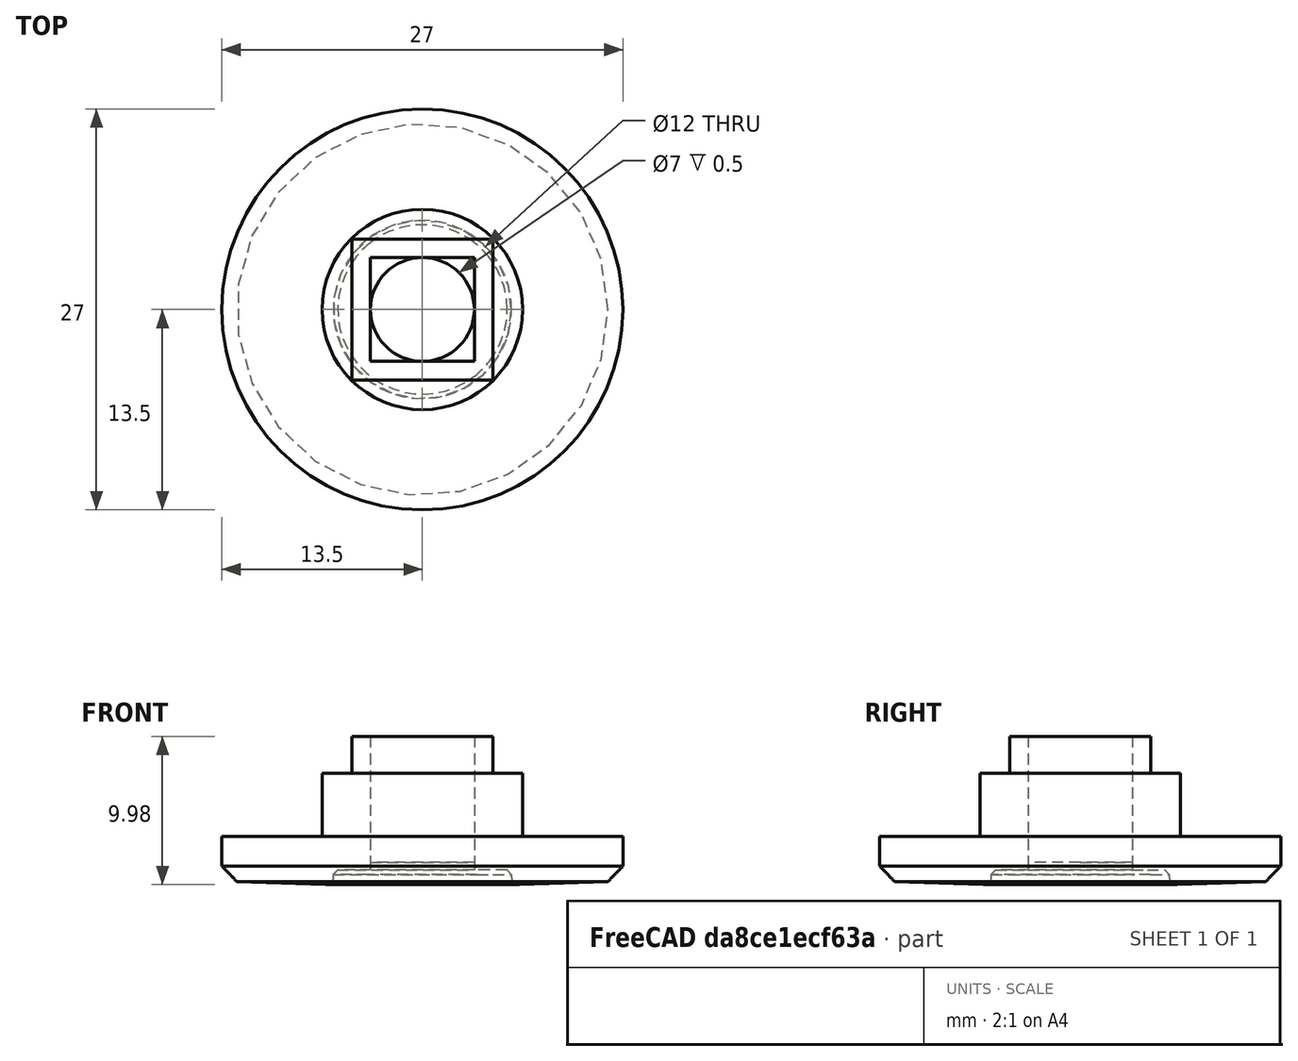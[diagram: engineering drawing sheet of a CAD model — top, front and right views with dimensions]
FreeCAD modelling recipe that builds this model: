
FCSTD DOCUMENT  (FreeCAD 0.19R24276 (Git))
Label: espaciador alojamiento junta goma
License: All rights reserved
LicenseURL: http://en.wikipedia.org/wiki/All_rights_reserved
objects: TechDraw::DrawViewDimension×10, TechDraw::DrawProjGroupItem×3, Part::Box×2, Part::Cut×2, Part::Chamfer×2, TechDraw::DrawSVGTemplate×2, TechDraw::DrawViewPart×2, TechDraw::DrawPage×2, Sketcher::SketchObject×1, PartDesign::Revolution×1, Part::MultiFuse×1, Part::Cylinder×1, Part::Fillet×1, TechDraw::DrawProjGroup×1, TechDraw::DrawViewAnnotation×1
note: 12 computed .brp shape members not serialized (recipe doc carries the construction recipe); baked Part::Feature solids carry a one-line shape summary decoded from their .brp

FEATURE [Sketcher::SketchObject] Sketch
  FullyConstrained = false
  MapMode = 5
  Placement = pos=(0,0,0) rot=(1,0,0;1.5708rad)
  sketch-geometry (8):
    g0: LineSegment StartX=0 StartY=0 StartZ=0 EndX=0 EndY=6.5 EndZ=0
    g1: LineSegment StartX=0 StartY=6.5 StartZ=0 EndX=6 EndY=6.5 EndZ=0
    g2: LineSegment StartX=6 StartY=6.5 StartZ=0 EndX=6 EndY=7.5 EndZ=0
    g3: LineSegment StartX=6 StartY=7.5 StartZ=0 EndX=13.5 EndY=7.23809 EndZ=0
    g4: LineSegment StartX=13.5 StartY=7.23809 StartZ=0 EndX=13.5 EndY=4.23809 EndZ=0
    g5: LineSegment StartX=13.5 StartY=4.23809 StartZ=0 EndX=6.75 EndY=4.23809 EndZ=0
    g6: LineSegment StartX=6.75 StartY=4.23809 StartZ=0 EndX=6.75 EndY=0 EndZ=0
    g7: LineSegment StartX=6.75 StartY=0 StartZ=0 EndX=0 EndY=0 EndZ=0
  constraints (23):
    c: Coincident(g0,g1)
    c: Coincident(g1,g2)
    c: Coincident(g2,g3)
    c: Coincident(g3,g4)
    c: Coincident(g4,g5)
    c: Coincident(g5,g6)
    c: Coincident(g6,g7)
    c: Angle(g3,g4) = 1.6057
    c: Vertical(g4)
    c: Horizontal(g1)
    c: Vertical(g2)
    c: DistanceY(g4,g4) = 3
    c: DistanceY(g2,g2) = 1
    c: Coincident(g0,g7)
    c: Coincident(g0,g-1)
    c: Vertical(g0)
    c: Horizontal(g7)
    c: Vertical(g6)
    c: DistanceY(g0,g0) = 6.5
    c: DistanceX(g1,g1) = 6
    c: DistanceX(g7,g7) = 6.75
    c: DistanceX(g5,g5) = 6.75
    c: Horizontal(g5)
FEATURE [PartDesign::Revolution] Revolution
  AllowMultiFace = false
  Angle = 360
  Axis = (0,0,1)
  Base = (0,0,0)
  Placement = pos=(0,0,0) rot=(1,0,0;1.5708rad)
  Profile = -> Sketch
  ReferenceAxis = -> Sketch [V_Axis]
  Reversed = true
FEATURE [Part::Box] Box  label="Cubo"
  AttacherType = Attacher::AttachEngine3D
  Height = 9
  Length = 9.5
  Placement = pos=(-4.75,-4.75,-2.5) rot=(0,0,1;0rad)
  Width = 9.5
FEATURE [Part::MultiFuse] Fusion
  Shapes = -> [Revolution,Box]
FEATURE [Part::Cylinder] Cylinder  label="Cilindro"
  Angle = 360
  AttacherType = Attacher::AttachEngine3D
  Height = 13
  Placement = pos=(0,0,-5) rot=(0,0,1;0rad)
  Radius = 3.5
FEATURE [Part::Box] Box001  label="Cubo001"
  AttacherType = Attacher::AttachEngine3D
  Height = 10.5
  Length = 7
  Placement = pos=(-3.5,-3.5,-4.5) rot=(0,0,1;0rad)
  Width = 7
FEATURE [Part::Cut] Cut
  Base = -> Fusion
  Tool = -> Box001
FEATURE [Part::Cut] Cut001
  Base = -> Cut
  Tool = -> Cylinder
FEATURE [Part::Chamfer] Chamfer
  Base = -> Cut001
  Edges = 1 edges r=0.3: [Edge5]
FEATURE [Part::Fillet] Fillet
  Base = -> Chamfer
  Edges = 1 edges r=0.5: [Edge3]
FEATURE [Part::Chamfer] Chamfer001
  Base = -> Fillet
  Edges = 1 edges r=1: [Edge27]
  Placement = pos=(0,0,0) rot=(1,0,0;3.14159rad)
FEATURE [TechDraw::DrawSVGTemplate] Template
  EditableTexts = Designed_by_Name=<owner>; Drawing_number=001; FC-Date=-; FC-SC=1:1; FC-SH=3/10; FC-Title=Spacer_O-ring; Subtitle=Espaciador Junta; Weight=<100gr
  Height = 210
  Orientation = 1
  Width = 297
FEATURE [TechDraw::DrawSVGTemplate] Template001
  EditableTexts = Designed_by_Name=<owner>; Drawing_number=001; FC-Date=-; FC-SC=4:1; FC-SH=4/10; FC-Title=Spacer_O-ring; Subtitle=Espaciador Junta; Weight=<100gr
  Height = 210
  Orientation = 1
  Width = 297
FEATURE [TechDraw::DrawViewPart] View
  CoarseView = false
  Direction = (0.577,-0.577,0.577)
  Focus = 100
  HardHidden = false
  IsoCount = 0
  IsoHidden = false
  IsoVisible = false
  LockPosition = false
  Perspective = false
  Rotation = 0
  Scale = 4
  ScaleType = 0
  SeamHidden = false
  SeamVisible = true
  SmoothHidden = false
  SmoothVisible = true
  Source = -> [Chamfer001]
  X = 201.279
  XDirection = (0.707,0.707,0)
  Y = 128.725
FEATURE [TechDraw::DrawViewPart] View001
  CoarseView = false
  Direction = (0.577,-0.577,0.577)
  Focus = 100
  HardHidden = false
  IsoCount = 0
  IsoHidden = false
  IsoVisible = false
  LockPosition = false
  Perspective = false
  Rotation = 0
  Scale = 4
  ScaleType = 0
  SeamHidden = false
  SeamVisible = true
  SmoothHidden = false
  SmoothVisible = true
  Source = -> [Chamfer001]
  X = 136.032
  XDirection = (0.707,0.707,0)
  Y = 120.195
FEATURE [TechDraw::DrawProjGroupItem] ProjItem  label="Front"
  CoarseView = false
  Direction = (0,-1,0)
  Focus = 100
  HardHidden = false
  IsoCount = 0
  IsoHidden = false
  IsoVisible = false
  LockPosition = true
  Perspective = false
  Rotation = 0
  RotationVector = (1,0,0)
  ScaleType = 2
  SeamHidden = false
  SeamVisible = true
  SmoothHidden = false
  SmoothVisible = true
  Source = -> [Chamfer001]
  Type = 0
  X = 0
  XDirection = (1,0,0)
  Y = 0
FEATURE [TechDraw::DrawProjGroupItem] ProjItem002  label="Top"
  CoarseView = false
  Direction = (0,0,1)
  Focus = 100
  HardHidden = false
  IsoCount = 0
  IsoHidden = false
  IsoVisible = false
  LockPosition = false
  Perspective = false
  Rotation = 0
  RotationVector = (1,0,0)
  ScaleType = 2
  SeamHidden = false
  SeamVisible = true
  SmoothHidden = false
  SmoothVisible = true
  Source = -> [Chamfer001]
  Type = 4
  X = 0
  XDirection = (1,0,0)
  Y = -41.9911
FEATURE [TechDraw::DrawProjGroupItem] ProjItem003  label="Bottom"
  CoarseView = false
  Direction = (0,0,-1)
  Focus = 100
  HardHidden = false
  IsoCount = 0
  IsoHidden = false
  IsoVisible = false
  LockPosition = false
  Perspective = false
  Rotation = 0
  RotationVector = (1,0,0)
  ScaleType = 2
  SeamHidden = false
  SeamVisible = true
  SmoothHidden = false
  SmoothVisible = true
  Source = -> [Chamfer001]
  Type = 5
  X = 0
  XDirection = (1,0,0)
  Y = 42.0089
FEATURE [TechDraw::DrawProjGroup] ProjGroup
  Anchor = -> ProjItem
  AutoDistribute = true
  LockPosition = false
  ProjectionType = 0
  Rotation = 0
  ScaleType = 2
  Source = -> [Chamfer001]
  Views = -> [ProjItem,ProjItem002,ProjItem003]
  X = 74.1782
  Y = 116.144
  spacingX = 15
  spacingY = 15
FEATURE [TechDraw::DrawViewDimension] Dimension
  Arbitrary = false
  ArbitraryTolerances = false
  EqualTolerance = true
  FormatSpec = %.2f
  FormatSpecOverTolerance = %+.2f
  FormatSpecUnderTolerance = %+.2f
  Inverted = false
  LockPosition = false
  MeasureType = 1
  OverTolerance = 0
  References2D = -> [ProjItem]
  Rotation = 0
  ScaleType = 0
  TheoreticalExact = false
  Type = 1
  UnderTolerance = 0
  X = 0.778035
  Y = -10.1577
FEATURE [TechDraw::DrawViewDimension] Dimension001
  Arbitrary = false
  ArbitraryTolerances = false
  EqualTolerance = true
  FormatSpec = %.2f
  FormatSpecOverTolerance = %+.2f
  FormatSpecUnderTolerance = %+.2f
  Inverted = false
  LockPosition = false
  MeasureType = 1
  OverTolerance = 0
  References2D = -> [ProjItem]
  Rotation = 0
  ScaleType = 0
  TheoreticalExact = false
  Type = 2
  UnderTolerance = 0
  X = 26.1569
  Y = -13.9783
FEATURE [TechDraw::DrawViewDimension] Dimension002
  Arbitrary = false
  ArbitraryTolerances = false
  EqualTolerance = true
  FormatSpec = ⌀%.2f
  FormatSpecOverTolerance = %+.2f
  FormatSpecUnderTolerance = %+.2f
  Inverted = false
  LockPosition = false
  MeasureType = 1
  OverTolerance = 0
  References2D = -> [ProjItem003]
  Rotation = 0
  ScaleType = 0
  TheoreticalExact = false
  Type = 5
  UnderTolerance = 0
  X = 31.6184
  Y = 13.0483
FEATURE [TechDraw::DrawViewDimension] Dimension003
  Arbitrary = false
  ArbitraryTolerances = false
  EqualTolerance = true
  FormatSpec = ⌀%.2f
  FormatSpecOverTolerance = %+.2f
  FormatSpecUnderTolerance = %+.2f
  Inverted = false
  LockPosition = false
  MeasureType = 1
  OverTolerance = 0
  References2D = -> [ProjItem002]
  Rotation = 0
  ScaleType = 0
  TheoreticalExact = false
  Type = 5
  UnderTolerance = 0
  X = 35.9907
  Y = 10.2209
FEATURE [TechDraw::DrawPage] Page  label="Vistas"
  KeepUpdated = true
  NextBalloonIndex = 1
  ProjectionType = 0
  Template = -> Template
  Views = -> [View,ProjGroup,Dimension,Dimension001,Dimension002,Dimension003]
FEATURE [TechDraw::DrawViewDimension] Dimension004
  Arbitrary = false
  ArbitraryTolerances = false
  EqualTolerance = true
  FormatSpec = %.2f
  FormatSpecOverTolerance = %+.2f
  FormatSpecUnderTolerance = %+.2f
  Inverted = false
  LockPosition = false
  MeasureType = 1
  OverTolerance = 0
  References2D = -> [View001]
  Rotation = 0
  ScaleType = 0
  TheoreticalExact = false
  Type = 2
  UnderTolerance = 0
  X = 65.823
  Y = -25.1787
FEATURE [TechDraw::DrawViewDimension] Dimension005
  Arbitrary = false
  ArbitraryTolerances = false
  EqualTolerance = true
  FormatSpec = %.2f
  FormatSpecOverTolerance = %+.2f
  FormatSpecUnderTolerance = %+.2f
  Inverted = false
  LockPosition = false
  MeasureType = 1
  OverTolerance = 0
  References2D = -> [View001]
  Rotation = 0
  ScaleType = 0
  TheoreticalExact = false
  Type = 0
  UnderTolerance = 0
  X = -23.464
  Y = -0.184481
FEATURE [TechDraw::DrawViewDimension] Dimension006
  Arbitrary = false
  ArbitraryTolerances = false
  EqualTolerance = true
  FormatSpec = ⌀%.2f
  FormatSpecOverTolerance = %+.2f
  FormatSpecUnderTolerance = %+.2f
  Inverted = false
  LockPosition = false
  MeasureType = 1
  OverTolerance = 0
  References2D = -> [View001]
  Rotation = 0
  ScaleType = 0
  TheoreticalExact = false
  Type = 5
  UnderTolerance = 0
  X = -0.676407
  Y = 24.1252
FEATURE [TechDraw::DrawViewDimension] Dimension007
  Arbitrary = false
  ArbitraryTolerances = false
  EqualTolerance = true
  FormatSpec = %.2f
  FormatSpecOverTolerance = %+.2f
  FormatSpecUnderTolerance = %+.2f
  Inverted = false
  LockPosition = false
  MeasureType = 1
  OverTolerance = 0
  References2D = -> [View001]
  Rotation = 0
  ScaleType = 0
  TheoreticalExact = false
  Type = 0
  UnderTolerance = 0
  X = 19.4863
  Y = 48.4609
FEATURE [TechDraw::DrawViewDimension] Dimension008
  Arbitrary = false
  ArbitraryTolerances = false
  EqualTolerance = true
  FormatSpec = %.2f
  FormatSpecOverTolerance = %+.2f
  FormatSpecUnderTolerance = %+.2f
  Inverted = false
  LockPosition = false
  MeasureType = 1
  OverTolerance = 0
  References2D = -> [View001]
  Rotation = 0
  ScaleType = 0
  TheoreticalExact = false
  Type = 2
  UnderTolerance = 0
  X = 25.0712
  Y = -6.13542
FEATURE [TechDraw::DrawViewDimension] Dimension009
  Arbitrary = false
  ArbitraryTolerances = false
  EqualTolerance = true
  FormatSpec = %.2f
  FormatSpecOverTolerance = %+.2f
  FormatSpecUnderTolerance = %+.2f
  Inverted = false
  LockPosition = false
  MeasureType = 1
  OverTolerance = 0
  References2D = -> [View001]
  Rotation = 0
  ScaleType = 0
  TheoreticalExact = false
  Type = 2
  UnderTolerance = 0
  X = 35.7805
  Y = 18.3707
FEATURE [TechDraw::DrawViewAnnotation] Annotation
  Font = osifont
  LineSpace = 80
  LockPosition = false
  MaxWidth = -1
  Rotation = 0
  ScaleType = 0
  Text = Aproximate measurements: | Check with 3D piece
  TextSize = 5
  TextStyle = 0
  X = 65.1234
  Y = 64.4805
FEATURE [TechDraw::DrawPage] Page001  label="Cotas"
  KeepUpdated = true
  NextBalloonIndex = 1
  ProjectionType = 0
  Template = -> Template001
  Views = -> [View001,Dimension004,Dimension005,Dimension006,Dimension007,Dimension008,Dimension009,Annotation]
